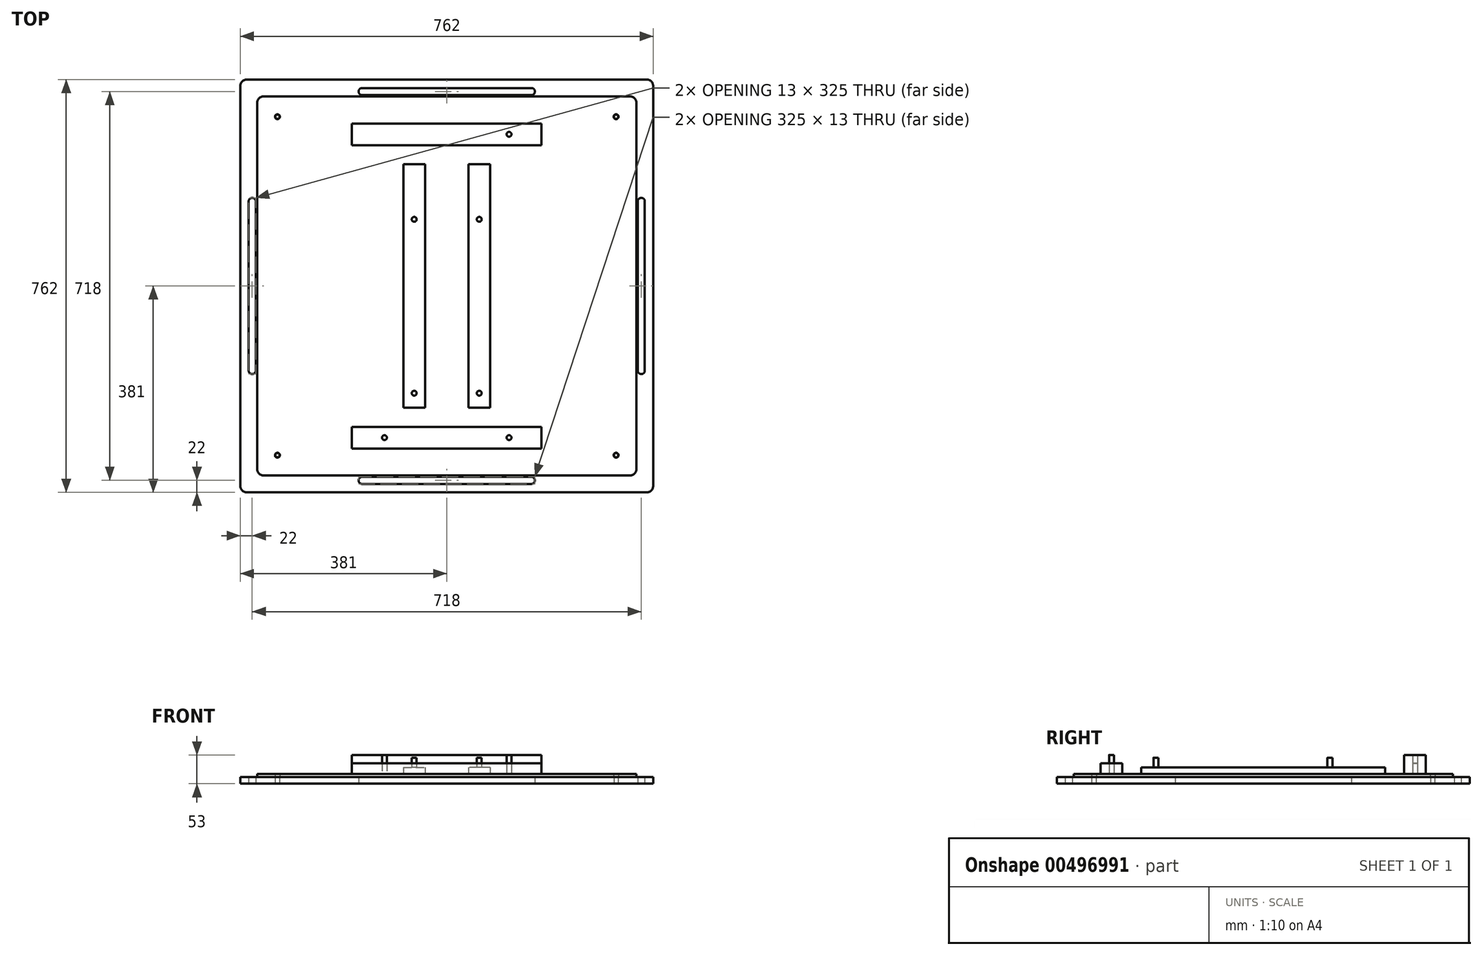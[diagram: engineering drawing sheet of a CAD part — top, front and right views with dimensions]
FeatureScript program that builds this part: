
annotation { "Feature Type Name" : "Feature", "Feature Type Description" : "" }
export const myFeature = defineFeature(function(context is Context, id is Id, definition is map)
    precondition{}
    {
        {
            var Q0;
            Q0=qCreatedBy(makeId("Top.planeOp"),FACE);
            var sketch = newSketch(context, id + "F0", { "sketchPlane" : qUnion([Q0])});
            skLineSegment(sketch, "E0.bottom", {"start": v(-369, 381) * mm, "end": v(369, 381) * mm});
            skLineSegment(sketch, "E0.top", {"start": v(-369, -381) * mm, "end": v(369, -381) * mm});
            skLineSegment(sketch, "E0.left", {"start": v(-381, 369) * mm, "end": v(-381, -369) * mm});
            skLineSegment(sketch, "E0.right", {"start": v(381, 369) * mm, "end": v(381, -369) * mm});
            skPoint(sketch, "E0.middle", {"position": v(0, 0) * mm});
            skLineSegment(sketch, "E1.0", {"start": v(-359, 359) * mm, "end": v(359, 359) * mm, "construction": true});
            skLineSegment(sketch, "E1.1", {"start": v(-359, 359) * mm, "end": v(-359, -359) * mm, "construction": true});
            skLineSegment(sketch, "E1.2", {"start": v(-359, -359) * mm, "end": v(359, -359) * mm, "construction": true});
            skLineSegment(sketch, "E1.3", {"start": v(359, 359) * mm, "end": v(359, -359) * mm, "construction": true});
            skLineSegment(sketch, "E2.bottom", {"start": v(-359.5, 162.5) * mm, "end": v(-358.5, 162.5) * mm});
            skLineSegment(sketch, "E2.top", {"start": v(-359.5, -162.5) * mm, "end": v(-358.5, -162.5) * mm});
            skLineSegment(sketch, "E2.left", {"start": v(-365.5, 156.5) * mm, "end": v(-365.5, -156.5) * mm});
            skLineSegment(sketch, "E2.right", {"start": v(-352.5, 156.5) * mm, "end": v(-352.5, -156.5) * mm});
            skPoint(sketch, "E2.middle", {"position": v(-359, 0) * mm});
            skLineSegment(sketch, "E3.MirrorCS", {"start": v(359.5, 162.5) * mm, "end": v(358.5, 162.5) * mm});
            skLineSegment(sketch, "E4.MirrorCS", {"start": v(359.5, -162.5) * mm, "end": v(358.5, -162.5) * mm});
            skLineSegment(sketch, "E5.MirrorCS", {"start": v(365.5, 156.5) * mm, "end": v(365.5, -156.5) * mm});
            skLineSegment(sketch, "E6.MirrorCS", {"start": v(352.5, 156.5) * mm, "end": v(352.5, -156.5) * mm});
            skPoint(sketch, "E7.MirrorP", {"position": v(359, 0) * mm});
            skLineSegment(sketch, "E8.bottom", {"start": v(-156.5, 365.5) * mm, "end": v(156.5, 365.5) * mm});
            skLineSegment(sketch, "E8.top", {"start": v(-156.5, 352.5) * mm, "end": v(156.5, 352.5) * mm});
            skLineSegment(sketch, "E8.left", {"start": v(-162.5, 359.5) * mm, "end": v(-162.5, 358.5) * mm});
            skLineSegment(sketch, "E8.right", {"start": v(162.5, 359.5) * mm, "end": v(162.5, 358.5) * mm});
            skPoint(sketch, "E8.middle", {"position": v(0, 359) * mm});
            skPoint(sketch, "E9.visualSharp", {"position": v(-365.5, 162.5) * mm});
            skArc(sketch, "E9.filletArc", {"start": v(-359.5, 162.5) * mm, "mid": v(-363.74, 160.74) * mm, "end": v(-365.5, 156.5) * mm});
            skPoint(sketch, "E10.visualSharp", {"position": v(-352.5, 162.5) * mm});
            skArc(sketch, "E10.filletArc", {"start": v(-352.5, 156.5) * mm, "mid": v(-354.26, 160.74) * mm, "end": v(-358.5, 162.5) * mm});
            skPoint(sketch, "E11.visualSharp", {"position": v(-365.5, -162.5) * mm});
            skArc(sketch, "E11.filletArc", {"start": v(-365.5, -156.5) * mm, "mid": v(-363.74, -160.74) * mm, "end": v(-359.5, -162.5) * mm});
            skPoint(sketch, "E12.visualSharp", {"position": v(-352.5, -162.5) * mm});
            skArc(sketch, "E12.filletArc", {"start": v(-358.5, -162.5) * mm, "mid": v(-354.26, -160.74) * mm, "end": v(-352.5, -156.5) * mm});
            skPoint(sketch, "E13.visualSharp", {"position": v(-162.5, 365.5) * mm});
            skArc(sketch, "E13.filletArc", {"start": v(-156.5, 365.5) * mm, "mid": v(-160.74, 363.74) * mm, "end": v(-162.5, 359.5) * mm});
            skPoint(sketch, "E14.visualSharp", {"position": v(-162.5, 352.5) * mm});
            skArc(sketch, "E14.filletArc", {"start": v(-162.5, 358.5) * mm, "mid": v(-160.74, 354.26) * mm, "end": v(-156.5, 352.5) * mm});
            skPoint(sketch, "E15.visualSharp", {"position": v(162.5, 365.5) * mm});
            skArc(sketch, "E15.filletArc", {"start": v(162.5, 359.5) * mm, "mid": v(160.74, 363.74) * mm, "end": v(156.5, 365.5) * mm});
            skPoint(sketch, "E16.visualSharp", {"position": v(162.5, 352.5) * mm});
            skArc(sketch, "E16.filletArc", {"start": v(156.5, 352.5) * mm, "mid": v(160.74, 354.26) * mm, "end": v(162.5, 358.5) * mm});
            skPoint(sketch, "E17.visualSharp", {"position": v(352.5, 162.5) * mm});
            skArc(sketch, "E17.filletArc", {"start": v(358.5, 162.5) * mm, "mid": v(354.26, 160.74) * mm, "end": v(352.5, 156.5) * mm});
            skPoint(sketch, "E18.visualSharp", {"position": v(365.5, 162.5) * mm});
            skArc(sketch, "E18.filletArc", {"start": v(365.5, 156.5) * mm, "mid": v(363.74, 160.74) * mm, "end": v(359.5, 162.5) * mm});
            skPoint(sketch, "E19.visualSharp", {"position": v(365.5, -162.5) * mm});
            skArc(sketch, "E19.filletArc", {"start": v(359.5, -162.5) * mm, "mid": v(363.74, -160.74) * mm, "end": v(365.5, -156.5) * mm});
            skPoint(sketch, "E20.visualSharp", {"position": v(352.5, -162.5) * mm});
            skArc(sketch, "E20.filletArc", {"start": v(352.5, -156.5) * mm, "mid": v(354.26, -160.74) * mm, "end": v(358.5, -162.5) * mm});
            skLineSegment(sketch, "E21.MirrorCS", {"start": v(-162.5, -359.5) * mm, "end": v(-162.5, -358.5) * mm});
            skArc(sketch, "E22.MirrorCS", {"start": v(162.5, -359.5) * mm, "mid": v(160.74, -363.74) * mm, "end": v(156.5, -365.5) * mm});
            skLineSegment(sketch, "E23.MirrorCS", {"start": v(162.5, -359.5) * mm, "end": v(162.5, -358.5) * mm});
            skArc(sketch, "E24.MirrorCS", {"start": v(-162.5, -358.5) * mm, "mid": v(-160.74, -354.26) * mm, "end": v(-156.5, -352.5) * mm});
            skArc(sketch, "E25.MirrorCS", {"start": v(-156.5, -365.5) * mm, "mid": v(-160.74, -363.74) * mm, "end": v(-162.5, -359.5) * mm});
            skArc(sketch, "E26.MirrorCS", {"start": v(156.5, -352.5) * mm, "mid": v(160.74, -354.26) * mm, "end": v(162.5, -358.5) * mm});
            skPoint(sketch, "E27.MirrorP", {"position": v(162.5, -352.5) * mm});
            skPoint(sketch, "E28.MirrorP", {"position": v(-162.5, -352.5) * mm});
            skLineSegment(sketch, "E29.MirrorCS", {"start": v(-156.5, -352.5) * mm, "end": v(156.5, -352.5) * mm});
            skLineSegment(sketch, "E30.MirrorCS", {"start": v(-156.5, -365.5) * mm, "end": v(156.5, -365.5) * mm});
            skPoint(sketch, "E31.MirrorP", {"position": v(162.5, -365.5) * mm});
            skPoint(sketch, "E32.MirrorP", {"position": v(0, -359) * mm});
            skPoint(sketch, "E33.MirrorP", {"position": v(-162.5, -365.5) * mm});
            skPoint(sketch, "E34.visualSharp", {"position": v(381, 381) * mm});
            skArc(sketch, "E34.filletArc", {"start": v(381, 369) * mm, "mid": v(377.49, 377.49) * mm, "end": v(369, 381) * mm});
            skPoint(sketch, "E35.visualSharp", {"position": v(381, -381) * mm});
            skArc(sketch, "E35.filletArc", {"start": v(369, -381) * mm, "mid": v(377.49, -377.49) * mm, "end": v(381, -369) * mm});
            skPoint(sketch, "E36.visualSharp", {"position": v(-381, -381) * mm});
            skArc(sketch, "E36.filletArc", {"start": v(-381, -369) * mm, "mid": v(-377.49, -377.49) * mm, "end": v(-369, -381) * mm});
            skPoint(sketch, "E37.visualSharp", {"position": v(-381, 381) * mm});
            skArc(sketch, "E37.filletArc", {"start": v(-369, 381) * mm, "mid": v(-377.49, 377.49) * mm, "end": v(-381, 369) * mm});
            skLineSegment(sketch, "E38.bottom", {"start": v(-312.5, 312.5) * mm, "end": v(312.5, 312.5) * mm, "construction": true});
            skLineSegment(sketch, "E38.top", {"start": v(-312.5, -312.5) * mm, "end": v(312.5, -312.5) * mm, "construction": true});
            skLineSegment(sketch, "E38.left", {"start": v(-312.5, 312.5) * mm, "end": v(-312.5, -312.5) * mm, "construction": true});
            skLineSegment(sketch, "E38.right", {"start": v(312.5, 312.5) * mm, "end": v(312.5, -312.5) * mm, "construction": true});
            skCircle(sketch, "E39", {"center": v(-312.5, 312.5) * mm, "radius": 4 * mm});
            skCircle(sketch, "E40", {"center": v(312.5, 312.5) * mm, "radius": 4 * mm});
            skCircle(sketch, "E41", {"center": v(312.5, -312.5) * mm, "radius": 4 * mm});
            skCircle(sketch, "E42", {"center": v(-312.5, -312.5) * mm, "radius": 4 * mm});
            skSolve(sketch);
        }
        {
            var Q0;
            Q0=makeQuery(id+"F0.imprint","IMPRINT",FACE,{"disambiguationData":[TD([[makeQuery(id+"F0.imprint","IMPRINT",EDGE,{"derivedFrom":sQuery(id+"F0.wireOp",EDGE,"E0.bottom")}),-1.0]])]});
            extrude(context, id + "F1", {"entities" : qUnion([Q0]), "depth" : 12 * mm});
        }
        {
            var Q0;
            Q0=makeQuery(id+"F1.opExtrude","CAP_FACE",FACE,{"disambiguationData":[OSD([sQuery(id+"F0.wireOp",EDGE,"E0.bottom"),sQuery(id+"F0.wireOp",EDGE,"E0.top"),sQuery(id+"F0.wireOp",EDGE,"E0.left"),sQuery(id+"F0.wireOp",EDGE,"E0.right"),sQuery(id+"F0.wireOp",EDGE,"E2.bottom"),sQuery(id+"F0.wireOp",EDGE,"E2.top"),sQuery(id+"F0.wireOp",EDGE,"E2.left"),sQuery(id+"F0.wireOp",EDGE,"E2.right"),sQuery(id+"F0.wireOp",EDGE,"E3.MirrorCS"),sQuery(id+"F0.wireOp",EDGE,"E4.MirrorCS"),sQuery(id+"F0.wireOp",EDGE,"E5.MirrorCS"),sQuery(id+"F0.wireOp",EDGE,"E6.MirrorCS"),sQuery(id+"F0.wireOp",EDGE,"E8.bottom"),sQuery(id+"F0.wireOp",EDGE,"E8.top"),sQuery(id+"F0.wireOp",EDGE,"E8.left"),sQuery(id+"F0.wireOp",EDGE,"E8.right"),sQuery(id+"F0.wireOp",EDGE,"E9.filletArc"),sQuery(id+"F0.wireOp",EDGE,"E10.filletArc"),sQuery(id+"F0.wireOp",EDGE,"E11.filletArc"),sQuery(id+"F0.wireOp",EDGE,"E12.filletArc"),sQuery(id+"F0.wireOp",EDGE,"E13.filletArc"),sQuery(id+"F0.wireOp",EDGE,"E14.filletArc"),sQuery(id+"F0.wireOp",EDGE,"E15.filletArc"),sQuery(id+"F0.wireOp",EDGE,"E16.filletArc"),sQuery(id+"F0.wireOp",EDGE,"E17.filletArc"),sQuery(id+"F0.wireOp",EDGE,"E18.filletArc"),sQuery(id+"F0.wireOp",EDGE,"E19.filletArc"),sQuery(id+"F0.wireOp",EDGE,"E20.filletArc"),sQuery(id+"F0.wireOp",EDGE,"E21.MirrorCS"),sQuery(id+"F0.wireOp",EDGE,"E22.MirrorCS"),sQuery(id+"F0.wireOp",EDGE,"E23.MirrorCS"),sQuery(id+"F0.wireOp",EDGE,"E24.MirrorCS"),sQuery(id+"F0.wireOp",EDGE,"E25.MirrorCS"),sQuery(id+"F0.wireOp",EDGE,"E26.MirrorCS"),sQuery(id+"F0.wireOp",EDGE,"E29.MirrorCS"),sQuery(id+"F0.wireOp",EDGE,"E30.MirrorCS"),sQuery(id+"F0.wireOp",EDGE,"E34.filletArc"),sQuery(id+"F0.wireOp",EDGE,"E35.filletArc"),sQuery(id+"F0.wireOp",EDGE,"E36.filletArc"),sQuery(id+"F0.wireOp",EDGE,"E37.filletArc"),sQuery(id+"F0.wireOp",EDGE,"E39"),sQuery(id+"F0.wireOp",EDGE,"E40"),sQuery(id+"F0.wireOp",EDGE,"E41"),sQuery(id+"F0.wireOp",EDGE,"E42")])],"isStart":false});
            var sketch = newSketch(context, id + "F2", { "sketchPlane" : qUnion([Q0])});
            skLineSegment(sketch, "E43.bottom", {"start": v(-338, 350) * mm, "end": v(338, 350) * mm});
            skLineSegment(sketch, "E43.top", {"start": v(-338, -350) * mm, "end": v(338, -350) * mm});
            skLineSegment(sketch, "E43.left", {"start": v(-350, 338) * mm, "end": v(-350, -338) * mm});
            skLineSegment(sketch, "E43.right", {"start": v(350, 338) * mm, "end": v(350, -338) * mm});
            skPoint(sketch, "E43.middle", {"position": v(0, 0) * mm});
            skCircle(sketch, "E44", {"center": v(-312.5, 312.5) * mm, "radius": 4.5 * mm});
            skCircle(sketch, "E45", {"center": v(312.5, 312.5) * mm, "radius": 4.5 * mm});
            skCircle(sketch, "E46", {"center": v(-312.5, -312.5) * mm, "radius": 4.5 * mm});
            skCircle(sketch, "E47", {"center": v(312.5, -312.5) * mm, "radius": 4.5 * mm});
            skPoint(sketch, "E48.visualSharp", {"position": v(-350, 350) * mm});
            skArc(sketch, "E48.filletArc", {"start": v(-338, 350) * mm, "mid": v(-346.49, 346.49) * mm, "end": v(-350, 338) * mm});
            skPoint(sketch, "E49.visualSharp", {"position": v(350, 350) * mm});
            skArc(sketch, "E49.filletArc", {"start": v(350, 338) * mm, "mid": v(346.49, 346.49) * mm, "end": v(338, 350) * mm});
            skPoint(sketch, "E50.visualSharp", {"position": v(350, -350) * mm});
            skArc(sketch, "E50.filletArc", {"start": v(338, -350) * mm, "mid": v(346.49, -346.49) * mm, "end": v(350, -338) * mm});
            skPoint(sketch, "E51.visualSharp", {"position": v(-350, -350) * mm});
            skArc(sketch, "E51.filletArc", {"start": v(-350, -338) * mm, "mid": v(-346.49, -346.49) * mm, "end": v(-338, -350) * mm});
            skSolve(sketch);
        }
        {
            var Q0;
            Q0 = qSketchRegion(id + "F2", true);
            extrude(context, id + "F3", {"entities" : qUnion([Q0]), "depth" : 6 * mm});
        }
        {
            var Q0;
            Q0=makeQuery(id+"F3.opExtrude","CAP_FACE",FACE,{"disambiguationData":[OSD([sQuery(id+"F2.wireOp",EDGE,"E43.bottom"),sQuery(id+"F2.wireOp",EDGE,"E43.top"),sQuery(id+"F2.wireOp",EDGE,"E43.left"),sQuery(id+"F2.wireOp",EDGE,"E43.right"),sQuery(id+"F2.wireOp",EDGE,"E44"),sQuery(id+"F2.wireOp",EDGE,"E45"),sQuery(id+"F2.wireOp",EDGE,"E46"),sQuery(id+"F2.wireOp",EDGE,"E47"),sQuery(id+"F2.wireOp",EDGE,"E48.filletArc"),sQuery(id+"F2.wireOp",EDGE,"E49.filletArc"),sQuery(id+"F2.wireOp",EDGE,"E50.filletArc"),sQuery(id+"F2.wireOp",EDGE,"E51.filletArc")])],"isStart":false});
            var sketch = newSketch(context, id + "F4", { "sketchPlane" : qUnion([Q0])});
            skLineSegment(sketch, "E52.bottom", {"start": v(-115, 280) * mm, "end": v(115, 280) * mm, "construction": true});
            skLineSegment(sketch, "E52.top", {"start": v(-115, -280) * mm, "end": v(115, -280) * mm, "construction": true});
            skLineSegment(sketch, "E52.left", {"start": v(-115, 280) * mm, "end": v(-115, -280) * mm, "construction": true});
            skLineSegment(sketch, "E52.right", {"start": v(115, 280) * mm, "end": v(115, -280) * mm, "construction": true});
            skPoint(sketch, "E52.middle", {"position": v(0, 0) * mm});
            skLineSegment(sketch, "E53.bottom", {"start": v(-175, 300) * mm, "end": v(175, 300) * mm});
            skLineSegment(sketch, "E53.top", {"start": v(-175, 260) * mm, "end": v(175, 260) * mm});
            skLineSegment(sketch, "E53.left", {"start": v(-175, 300) * mm, "end": v(-175, 260) * mm});
            skLineSegment(sketch, "E53.right", {"start": v(175, 300) * mm, "end": v(175, 260) * mm});
            skPoint(sketch, "E53.middle", {"position": v(0, 280) * mm});
            skCircle(sketch, "E54", {"center": v(-115, 280) * mm, "radius": 4.5 * mm});
            skCircle(sketch, "E55", {"center": v(115, 280) * mm, "radius": 4.5 * mm});
            skLineSegment(sketch, "E56.MirrorCS", {"start": v(175, 260) * mm, "end": v(175, 300) * mm});
            skLineSegment(sketch, "E57.MirrorCS", {"start": v(-175, 260) * mm, "end": v(-175, 300) * mm});
            skLineSegment(sketch, "E58.bottom", {"start": v(-175, -260) * mm, "end": v(175, -260) * mm});
            skLineSegment(sketch, "E58.top", {"start": v(-175, -300) * mm, "end": v(175, -300) * mm});
            skLineSegment(sketch, "E58.left", {"start": v(-175, -260) * mm, "end": v(-175, -300) * mm});
            skLineSegment(sketch, "E58.right", {"start": v(175, -260) * mm, "end": v(175, -300) * mm});
            skPoint(sketch, "E58.middle", {"position": v(0, -280) * mm});
            skCircle(sketch, "E59", {"center": v(-115, -280) * mm, "radius": 4.5 * mm});
            skCircle(sketch, "E60", {"center": v(115, -280) * mm, "radius": 4.5 * mm});
            skLineSegment(sketch, "E61", {"start": v(-198.23, 123) * mm, "end": v(235.67, 123) * mm, "construction": true});
            skLineSegment(sketch, "E62", {"start": v(-193.08, -198) * mm, "end": v(247.25, -198) * mm, "construction": true});
            skLineSegment(sketch, "E63", {"start": v(-60, 169.17) * mm, "end": v(-60, -233.83) * mm, "construction": true});
            skLineSegment(sketch, "E64", {"start": v(60, 170.46) * mm, "end": v(60, -231.25) * mm, "construction": true});
            skLineSegment(sketch, "E65.bottom", {"start": v(-80, 225) * mm, "end": v(-40, 225) * mm});
            skLineSegment(sketch, "E65.top", {"start": v(-80, -225) * mm, "end": v(-40, -225) * mm});
            skLineSegment(sketch, "E65.left", {"start": v(-80, 225) * mm, "end": v(-80, -225) * mm});
            skLineSegment(sketch, "E65.right", {"start": v(-40, 225) * mm, "end": v(-40, -225) * mm});
            skPoint(sketch, "E65.middle", {"position": v(-60, 0) * mm});
            skLineSegment(sketch, "E66.MirrorCS", {"start": v(80, -225) * mm, "end": v(40, -225) * mm});
            skLineSegment(sketch, "E67.MirrorCS", {"start": v(40, 225) * mm, "end": v(40, -225) * mm});
            skLineSegment(sketch, "E68.MirrorCS", {"start": v(80, 225) * mm, "end": v(80, -225) * mm});
            skLineSegment(sketch, "E69.MirrorCS", {"start": v(80, 225) * mm, "end": v(40, 225) * mm});
            skCircle(sketch, "E70", {"center": v(-60, 123) * mm, "radius": 4.5 * mm});
            skCircle(sketch, "E71", {"center": v(60, 123) * mm, "radius": 4.5 * mm});
            skCircle(sketch, "E72", {"center": v(60, -198) * mm, "radius": 4.5 * mm});
            skCircle(sketch, "E73", {"center": v(-60, -198) * mm, "radius": 4.5 * mm});
            skSolve(sketch);
        }
        {
            var Q0;
            Q0=makeQuery(id+"F4.imprint","IMPRINT",FACE,{"disambiguationData":[TD([[makeQuery(id+"F4.imprint","IMPRINT",EDGE,{"derivedFrom":sQuery(id+"F4.wireOp",EDGE,"E55")}),1.0]])]});
            var Q1;
            Q1=makeQuery(id+"F4.imprint","IMPRINT",FACE,{"disambiguationData":[TD([[makeQuery(id+"F4.imprint","IMPRINT",EDGE,{"derivedFrom":sQuery(id+"F4.wireOp",EDGE,"E58.bottom")}),-1.0]])]});
            extrude(context, id + "F5", {"entities" : qUnion([Q0, Q1]), "depth" : 20 * mm});
        }
        {
            var Q0;
            Q0=makeQuery(id+"F4.imprint","IMPRINT",FACE,{"disambiguationData":[TD([[makeQuery(id+"F4.imprint","IMPRINT",EDGE,{"derivedFrom":sQuery(id+"F4.wireOp",EDGE,"E65.bottom")}),-1.0]])]});
            var Q1;
            Q1=makeQuery(id+"F4.imprint","IMPRINT",FACE,{"disambiguationData":[TD([[makeQuery(id+"F4.imprint","IMPRINT",EDGE,{"derivedFrom":sQuery(id+"F4.wireOp",EDGE,"E66.MirrorCS")}),-1.0]])]});
            extrude(context, id + "F6", {"entities" : qUnion([Q0, Q1]), "depth" : 12 * mm});
        }
        {
            var Q0;
            Q0=makeQuery(id+"F4.imprint","IMPRINT",FACE,{"disambiguationData":[TD([[makeQuery(id+"F4.imprint","IMPRINT",EDGE,{"derivedFrom":sQuery(id+"F4.wireOp",EDGE,"E54")}),1.0]])]});
            var Q1;
            Q1=makeQuery(id+"F4.imprint","IMPRINT",FACE,{"disambiguationData":[TD([[makeQuery(id+"F4.imprint","IMPRINT",EDGE,{"derivedFrom":sQuery(id+"F4.wireOp",EDGE,"E55")}),-1.0]])]});
            var Q2;
            Q2=makeQuery(id+"F4.imprint","IMPRINT",FACE,{"disambiguationData":[TD([[makeQuery(id+"F4.imprint","IMPRINT",EDGE,{"derivedFrom":sQuery(id+"F4.wireOp",EDGE,"E59")}),1.0]])]});
            var Q3;
            Q3=makeQuery(id+"F4.imprint","IMPRINT",FACE,{"disambiguationData":[TD([[makeQuery(id+"F4.imprint","IMPRINT",EDGE,{"derivedFrom":sQuery(id+"F4.wireOp",EDGE,"E60")}),1.0]])]});
            extrude(context, id + "F7", {"entities" : qUnion([Q0, Q1, Q2, Q3]), "depth" : 35 * mm});
        }
        {
            var Q0;
            Q0=makeQuery(id+"F4.imprint","IMPRINT",FACE,{"disambiguationData":[TD([[makeQuery(id+"F4.imprint","IMPRINT",EDGE,{"derivedFrom":sQuery(id+"F4.wireOp",EDGE,"E70")}),1.0]])]});
            var Q1;
            Q1=makeQuery(id+"F4.imprint","IMPRINT",FACE,{"disambiguationData":[TD([[makeQuery(id+"F4.imprint","IMPRINT",EDGE,{"derivedFrom":sQuery(id+"F4.wireOp",EDGE,"E71")}),1.0]])]});
            var Q2;
            Q2=makeQuery(id+"F4.imprint","IMPRINT",FACE,{"disambiguationData":[TD([[makeQuery(id+"F4.imprint","IMPRINT",EDGE,{"derivedFrom":sQuery(id+"F4.wireOp",EDGE,"E73")}),1.0]])]});
            var Q3;
            Q3=makeQuery(id+"F4.imprint","IMPRINT",FACE,{"disambiguationData":[TD([[makeQuery(id+"F4.imprint","IMPRINT",EDGE,{"derivedFrom":sQuery(id+"F4.wireOp",EDGE,"E72")}),1.0]])]});
            extrude(context, id + "F8", {"entities" : qUnion([Q0, Q1, Q2, Q3]), "operationType" : NewBodyOperationType.ADD, "depth" : 30 * mm});
        }
    });
